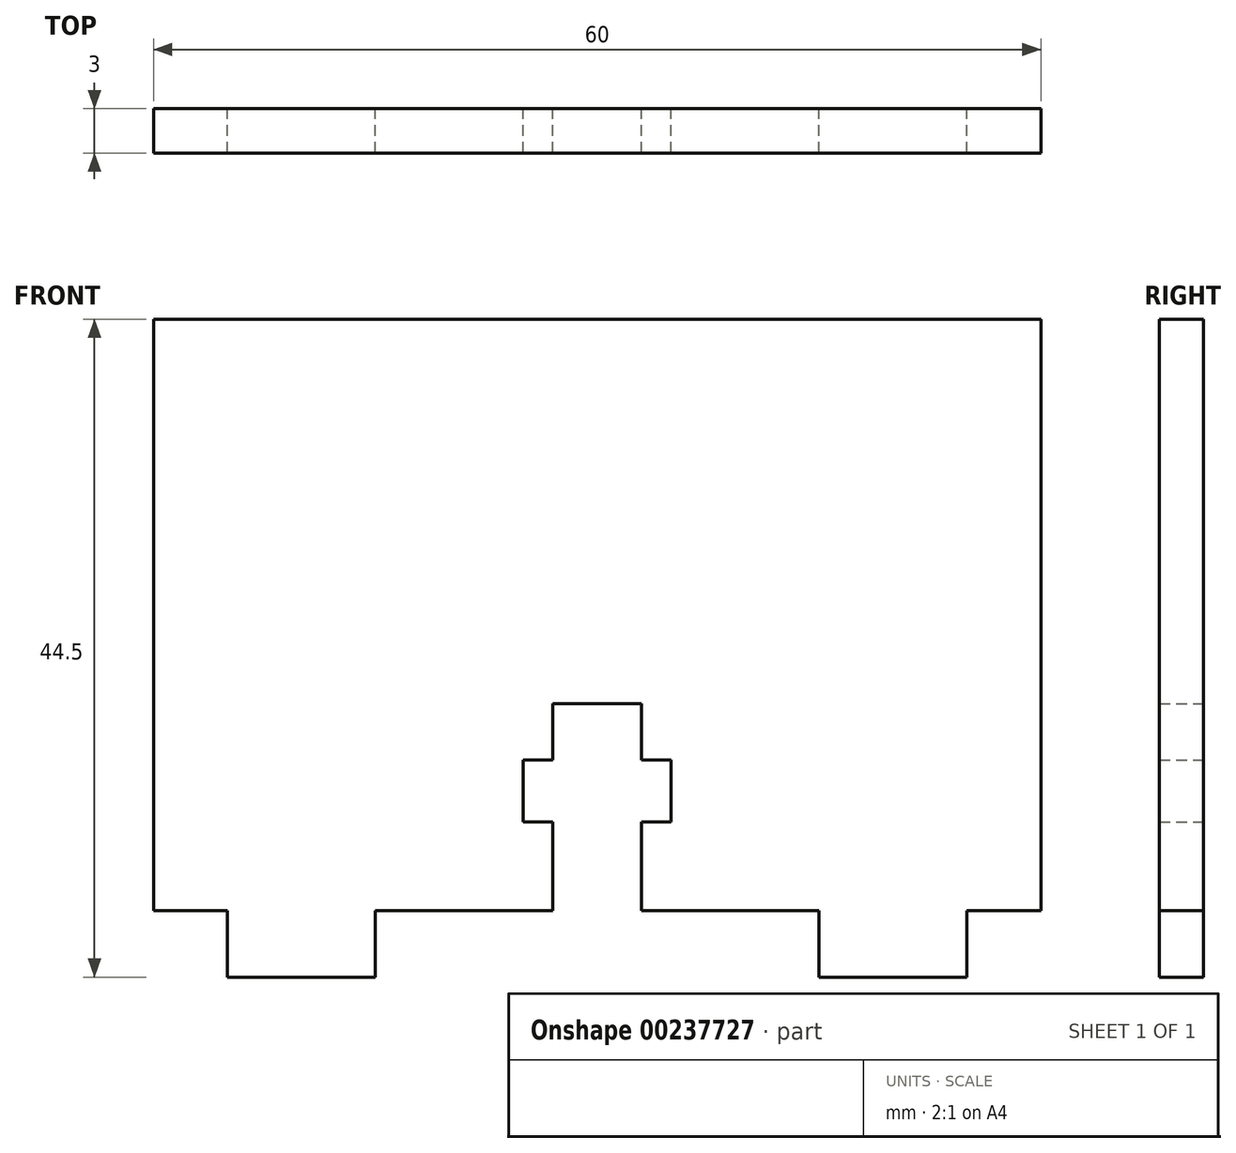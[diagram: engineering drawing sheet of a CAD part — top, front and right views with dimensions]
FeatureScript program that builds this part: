
annotation { "Feature Type Name" : "Feature", "Feature Type Description" : "" }
export const myFeature = defineFeature(function(context is Context, id is Id, definition is map)
    precondition{}
    {
        {
            var Q0;
            Q0=qCreatedBy(makeId("Front.planeOp"),FACE);
            var sketch = newSketch(context, id + "F0", { "sketchPlane" : qUnion([Q0])});
            skLineSegment(sketch, "E0.bottom", {"start": v(-30, 0) * mm, "end": v(-25, 0) * mm});
            skLineSegment(sketch, "E0.top", {"start": v(-30, 40) * mm, "end": v(30, 40) * mm});
            skLineSegment(sketch, "E0.left", {"start": v(-30, 0) * mm, "end": v(-30, 40) * mm});
            skLineSegment(sketch, "E0.right", {"start": v(30, 0) * mm, "end": v(30, 40) * mm});
            skLineSegment(sketch, "E1.top", {"start": v(-25, -4.5) * mm, "end": v(-15, -4.5) * mm});
            skLineSegment(sketch, "E1.left", {"start": v(-25, 0) * mm, "end": v(-25, -4.5) * mm});
            skLineSegment(sketch, "E1.right", {"start": v(-15, 0) * mm, "end": v(-15, -4.5) * mm});
            skLineSegment(sketch, "E2.trimOffspring", {"start": v(-15, 0) * mm, "end": v(-3, 0) * mm});
            skLineSegment(sketch, "E3.MirrorCS", {"start": v(25, 0) * mm, "end": v(25, -4.5) * mm});
            skLineSegment(sketch, "E4.MirrorCS", {"start": v(25, -4.5) * mm, "end": v(15, -4.5) * mm});
            skLineSegment(sketch, "E5.MirrorCS", {"start": v(15, 0) * mm, "end": v(15, -4.5) * mm});
            skLineSegment(sketch, "E6.trimOffspring", {"start": v(25, 0) * mm, "end": v(30, 0) * mm});
            skLineSegment(sketch, "E7", {"start": v(-3, 0) * mm, "end": v(-3, 6) * mm});
            skLineSegment(sketch, "E8", {"start": v(-3, 6) * mm, "end": v(-5, 6) * mm});
            skLineSegment(sketch, "E9", {"start": v(-5, 6) * mm, "end": v(-5, 10.2) * mm});
            skLineSegment(sketch, "E10.MirrorCS", {"start": v(5, 6) * mm, "end": v(5, 10.2) * mm});
            skLineSegment(sketch, "E11.MirrorCS", {"start": v(3, 0) * mm, "end": v(3, 6) * mm});
            skLineSegment(sketch, "E12.MirrorCS", {"start": v(3, 6) * mm, "end": v(5, 6) * mm});
            skLineSegment(sketch, "E13", {"start": v(-5, 10.2) * mm, "end": v(5, 10.2) * mm});
            skLineSegment(sketch, "E14.trimOffspring", {"start": v(3, 0) * mm, "end": v(15, 0) * mm});
            skLineSegment(sketch, "E15.bottom", {"start": v(-3, 10.2) * mm, "end": v(3, 10.2) * mm});
            skLineSegment(sketch, "E15.top", {"start": v(-3, 14) * mm, "end": v(3, 14) * mm});
            skLineSegment(sketch, "E15.left", {"start": v(-3, 10.2) * mm, "end": v(-3, 14) * mm});
            skLineSegment(sketch, "E15.right", {"start": v(3, 10.2) * mm, "end": v(3, 14) * mm});
            skSolve(sketch);
        }
        {
            var Q0;
            Q0=makeQuery(id+"F0.imprint","IMPRINT",FACE,{"disambiguationData":[TD([[makeQuery(id+"F0.imprint","IMPRINT",EDGE,{"derivedFrom":sQuery(id+"F0.wireOp",EDGE,"E0.bottom")}),1.0]])]});
            extrude(context, id + "F1", {"entities" : qUnion([Q0]), "endBound" : BoundingType.SYMMETRIC, "depth" : 3 * mm});
        }
    });
